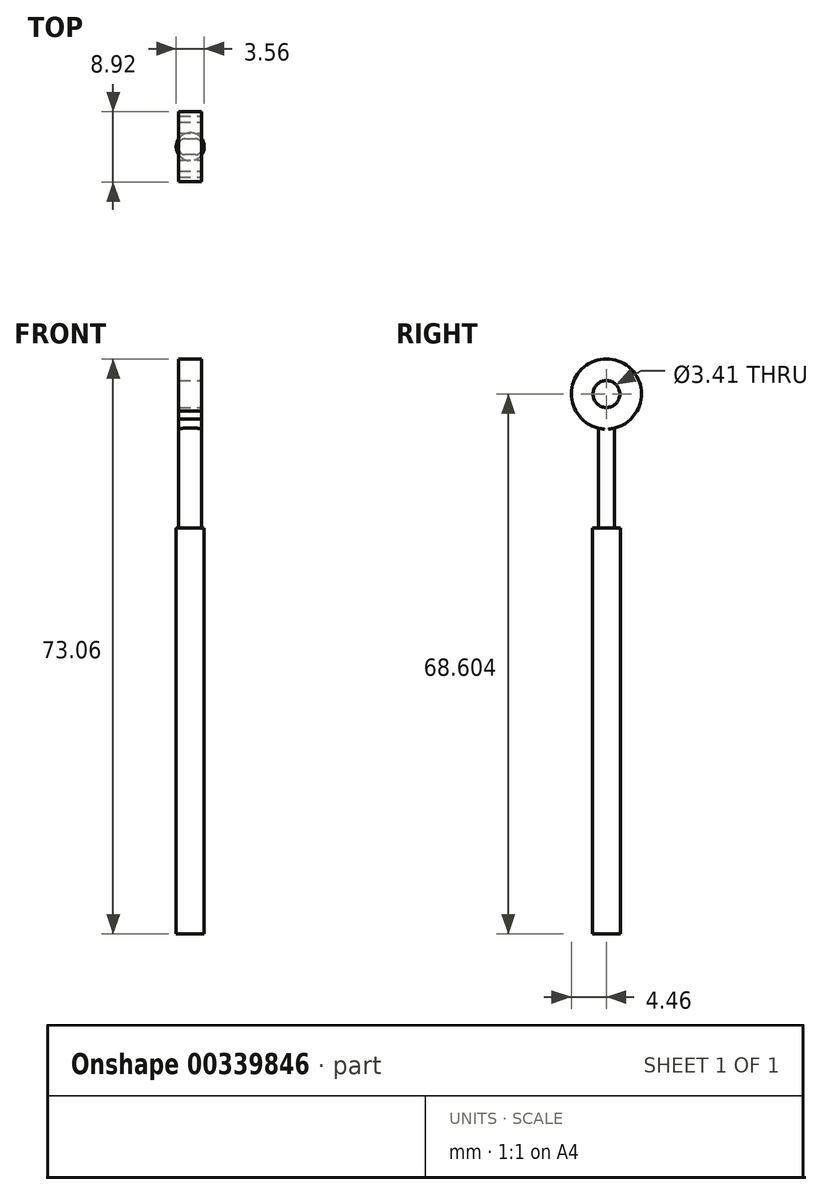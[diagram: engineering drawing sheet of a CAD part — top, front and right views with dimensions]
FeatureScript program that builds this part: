
annotation { "Feature Type Name" : "Feature", "Feature Type Description" : "" }
export const myFeature = defineFeature(function(context is Context, id is Id, definition is map)
    precondition{}
    {
        {
            var Q0;
            Q0=qCreatedBy(makeId("Top.planeOp"),FACE);
            var sketch = newSketch(context, id + "F0", { "sketchPlane" : qUnion([Q0])});
            skCircle(sketch, "E0", {"center": v(0, 0) * mm, "radius": 1.78 * mm});
            skSolve(sketch);
        }
        {
            var Q0;
            Q0=makeQuery(id+"F0.imprint","IMPRINT",FACE,{"disambiguationData":[TD([[makeQuery(id+"F0.imprint","IMPRINT",EDGE,{"derivedFrom":sQuery(id+"F0.wireOp",EDGE,"E0")}),1.0]])]});
            extrude(context, id + "F1", {"entities" : qUnion([Q0]), "depth" : 51.56 * mm});
        }
        {
            var Q0;
            Q0=makeQuery(id+"F1.opExtrude","CAP_FACE",FACE,{"disambiguationData":[OSD([sQuery(id+"F0.wireOp",EDGE,"E0")])],"isStart":false});
            var sketch = newSketch(context, id + "F2", { "sketchPlane" : qUnion([Q0])});
            skLineSegment(sketch, "E1", {"start": v(-1.46, 1.01) * mm, "end": v(1.46, 1.01) * mm});
            skLineSegment(sketch, "E2", {"start": v(1.46, 1.01) * mm, "end": v(1.46, -1.01) * mm});
            skLineSegment(sketch, "E3", {"start": v(1.46, -1.01) * mm, "end": v(-1.46, -1.01) * mm});
            skLineSegment(sketch, "E4", {"start": v(-1.46, -1.01) * mm, "end": v(-1.46, 1.01) * mm});
            skSolve(sketch);
        }
        {
            var Q0;
            Q0=makeQuery(id+"F2.imprint","IMPRINT",FACE,{"disambiguationData":[TD([[makeQuery(id+"F2.imprint","IMPRINT",EDGE,{"derivedFrom":sQuery(id+"F2.wireOp",EDGE,"E1")}),-1.0]])]});
            extrude(context, id + "F3", {"entities" : qUnion([Q0]), "operationType" : NewBodyOperationType.ADD, "depth" : 12.7 * mm});
        }
        {
            var Q0;
            Q0=makeQuery(id+"F3.opExtrude","SWEPT_FACE",FACE,{"disambiguationData":[OSD([sQuery(id+"F2.wireOp",EDGE,"E2")])]});
            var sketch = newSketch(context, id + "F4", { "sketchPlane" : qUnion([Q0])});
            skCircle(sketch, "E5", {"center": v(0, 68.6) * mm, "radius": 4.46 * mm});
            skFitSpline(sketch, "E6", {"points": [v(-1.01, 61.62) * mm, v(-1.89, 63.6) * mm, v(-3.88, 66.41) * mm], "startDerivative": vector(-1.62, 4.36) * mm, "endDerivative": vector(-4.02, 5.2) * mm});
            skFitSpline(sketch, "E7.MirrorCS", {"points": [v(1.01, 61.62) * mm, v(1.89, 63.6) * mm, v(3.88, 66.41) * mm], "startDerivative": vector(1.62, 4.36) * mm, "endDerivative": vector(4.02, 5.2) * mm});
            skPoint(sketch, "E8.start.orphan", {"position": v(0, 56.56) * mm});
            skLineSegment(sketch, "E9", {"start": v(-1.01, 61.62) * mm, "end": v(1.01, 61.62) * mm});
            skCircle(sketch, "E10", {"center": v(0, 68.6) * mm, "radius": 1.7 * mm});
            skSolve(sketch);
        }
        {
            var Q0;
            Q0=makeQuery(id+"F4.imprint","IMPRINT",FACE,{"disambiguationData":[TD([[makeQuery(id+"F4.imprint","IMPRINT",EDGE,{"derivedFrom":sQuery(id+"F4.wireOp",EDGE,"E10")}),-1.0]])]});
            extrude(context, id + "F5", {"entities" : qUnion([Q0]), "operationType" : NewBodyOperationType.ADD, "oppositeDirection" : true, "depth" : 2.92 * mm});
        }
        {
            var Q0;
            Q0=makeQuery(id+"F3.opExtrude","SWEPT_EDGE",EDGE,{"disambiguationData":[OSD([sQuery(id+"F0.wireOp",EDGE,"E0"),sQuery(id+"F2.wireOp",EDGE,"E2"),sQuery(id+"F2.wireOp",EDGE,"E3")])]});
            var Q1;
            Q1=makeQuery(id+"F3.opExtrude","SWEPT_EDGE",EDGE,{"disambiguationData":[OSD([sQuery(id+"F0.wireOp",EDGE,"E0"),sQuery(id+"F2.wireOp",EDGE,"E1"),sQuery(id+"F2.wireOp",EDGE,"E4")])]});
            var Q2;
            Q2=makeQuery(id+"F3.opExtrude","SWEPT_EDGE",EDGE,{"disambiguationData":[OSD([sQuery(id+"F0.wireOp",EDGE,"E0"),sQuery(id+"F2.wireOp",EDGE,"E1"),sQuery(id+"F2.wireOp",EDGE,"E2")])]});
            var Q3;
            Q3=makeQuery(id+"F3.opExtrude","SWEPT_EDGE",EDGE,{"disambiguationData":[OSD([sQuery(id+"F0.wireOp",EDGE,"E0"),sQuery(id+"F2.wireOp",EDGE,"E3"),sQuery(id+"F2.wireOp",EDGE,"E4")])]});
            fillet(context, id + "F6", {"entities" : qUnion([Q0, Q1, Q2, Q3]), "radius" : 0.76 * mm, "tangentPropagation" : true, "allowEdgeOverflow" : false});
        }
    });
